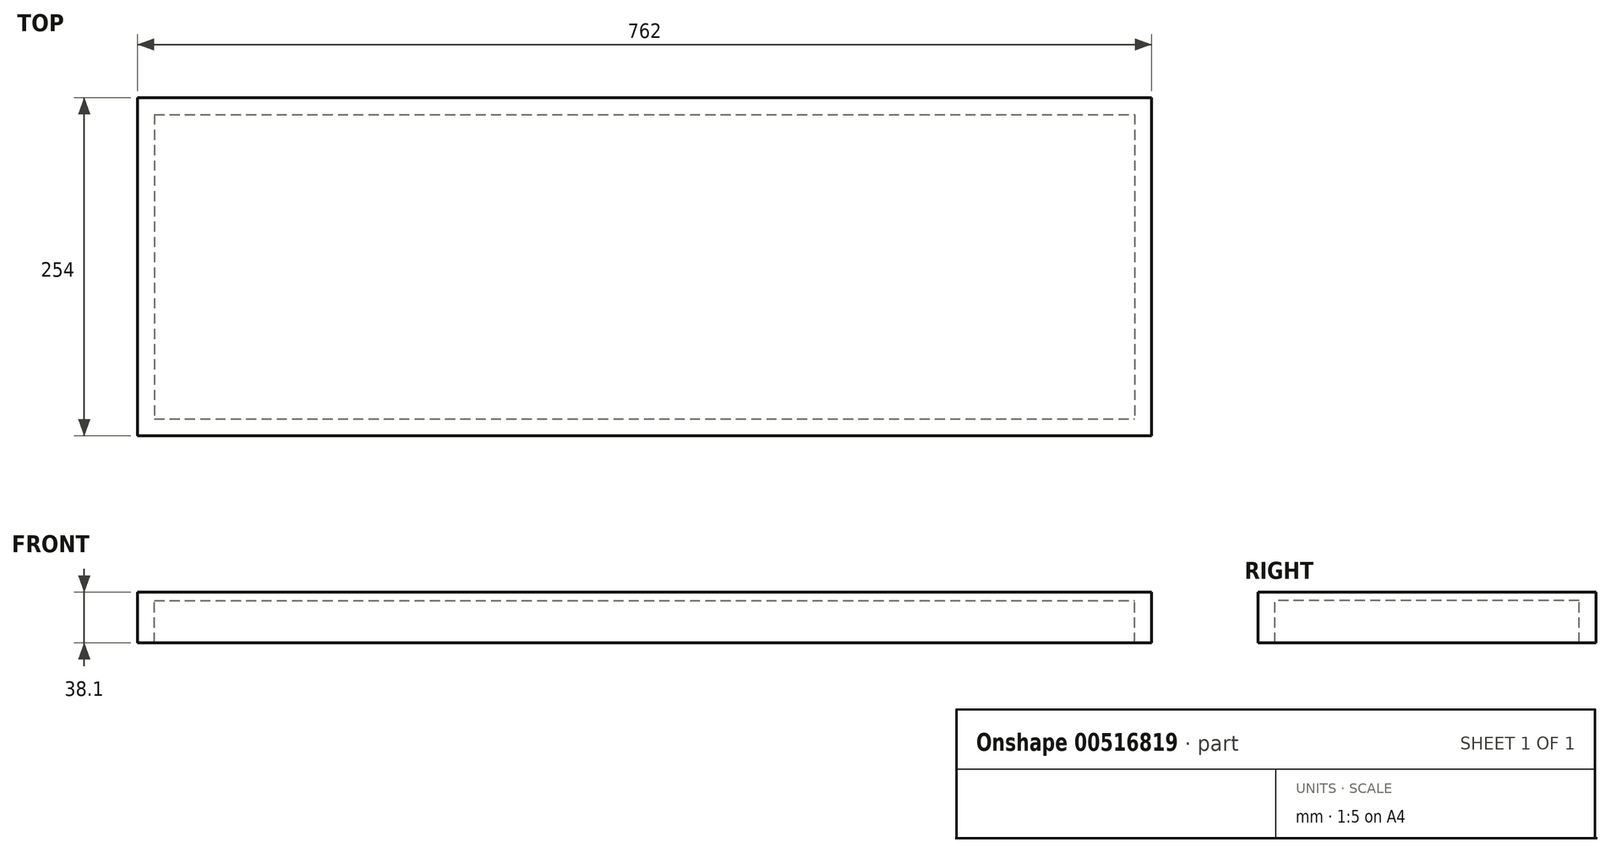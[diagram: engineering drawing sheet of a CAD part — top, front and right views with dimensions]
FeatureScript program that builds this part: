
annotation { "Feature Type Name" : "Feature", "Feature Type Description" : "" }
export const myFeature = defineFeature(function(context is Context, id is Id, definition is map)
    precondition{}
    {
        {
            var Q0;
            Q0=qCreatedBy(makeId("Top.planeOp"),FACE);
            var sketch = newSketch(context, id + "F0", { "sketchPlane" : qUnion([Q0])});
            skLineSegment(sketch, "E0.bottom", {"start": v(-133.15, 184.76) * mm, "end": v(628.85, 184.76) * mm});
            skLineSegment(sketch, "E0.top", {"start": v(-133.15, -69.24) * mm, "end": v(628.85, -69.24) * mm});
            skLineSegment(sketch, "E0.left", {"start": v(-133.15, 184.76) * mm, "end": v(-133.15, -69.24) * mm});
            skLineSegment(sketch, "E0.right", {"start": v(628.85, 184.76) * mm, "end": v(628.85, -69.24) * mm});
            skLineSegment(sketch, "E1.0", {"start": v(-120.45, 172.06) * mm, "end": v(-120.45, -56.54) * mm});
            skLineSegment(sketch, "E1.1", {"start": v(-120.45, 172.06) * mm, "end": v(616.15, 172.06) * mm});
            skLineSegment(sketch, "E1.2", {"start": v(616.15, 172.06) * mm, "end": v(616.15, -56.54) * mm});
            skLineSegment(sketch, "E1.3", {"start": v(-120.45, -56.54) * mm, "end": v(616.15, -56.54) * mm});
            skSolve(sketch);
        }
        {
            var Q0;
            Q0=makeQuery(id+"F0.imprint","IMPRINT",FACE,{"disambiguationData":[TD([[makeQuery(id+"F0.imprint","IMPRINT",EDGE,{"derivedFrom":sQuery(id+"F0.wireOp",EDGE,"E0.bottom")}),-1.0]])]});
            var Q1;
            Q1=makeQuery(id+"F0.imprint","IMPRINT",FACE,{"disambiguationData":[TD([[makeQuery(id+"F0.imprint","IMPRINT",EDGE,{"derivedFrom":sQuery(id+"F0.wireOp",EDGE,"E1.0")}),1.0]])]});
            extrude(context, id + "F1", {"entities" : qUnion([Q0, Q1]), "depth" : 6.35 * mm, "offsetDistance" : 25.4 * mm});
        }
        {
            var Q0;
            Q0 = qSketchRegion(id + "F0", true);
            extrude(context, id + "F2", {"entities" : qUnion([Q0]), "operationType" : NewBodyOperationType.ADD, "oppositeDirection" : true, "depth" : 31.75 * mm, "offsetDistance" : 25.4 * mm});
        }
    });
